# Revit family: Neo_Basin-Wall_Mounted-Neo_Metro-8936-EB
name_source: partatom
category: Plumbing Fixtures
units: mm (PartAtom-declared; Revit-internal decimal feet)

## family parameters
Cut with Voids When Loaded = No
Host = Face
OmniClass Number = 23.45.05.14.14
OmniClass Title = Sinks/Lavatories
Part Type = Normal
Room Calculation Point = No
Round Connector Dimension = Use Diameter
Shared = Yes

## types (1)
- 8936-EB
    8936 - NEO-BASIN (with NO Side Shelves), Satin Finish Stainless Steel = No
    8936-EB - NEO-BASIN with Enclosed Bottom, Entire Unit is Satin Finish Stainless Steel = Yes
    8936-HP - NEO-BASIN (with NO Side Shelves), Mira Finish Stainless Steel = No
    8936-HP-EB - NEO-BASIN with Enclosed Bottom, Entire Unit is Mira Finish Stainless Steel = No
    ADA Compliant = Yes
    Assembly Code = D2010440
    Basin Depth = 7"
    Basin Height = 5"
    Basin Width = 19"
    CW Connection = Yes
    CWFU = 1.5
    Cold Water Connection Diameter = 1/2"
    Compliance Certifications = ASME A112.18.1, CSA B125.1, cUPC
    Default Elevation = 34"
    Description = Neo-Basin Stainless Steel, Wall-Mounted Sink
    Finish = Stainless Steel-Neo Metro-Satin
    H0 - Less Punching (Will use wall-mounted faucet) = Yes
    H1 - Single Hole = No
    H38 - 8" (203mm) Center Set = No
    HW Connection = Yes
    HWFU = 1.5
    Hot Water Connection Diameter = 1/2"
    Installation Instruction Link = https://www.neo-metro.com
    Installation Type = Wall Mounted
    Manufacturer = Neo Metro
    Material = Stainless Steel-Neo Metro-Satin
    Model = 8936-EB
    OF - Option - Overflow Outlet = No
    Product Documentation Link = https://www.neo-metro.com
    Product Page URL = https://www.neo-metro.com
    Sink Back Height = 9 1/4"
    Sink Base Length = 6 1/2"
    Sink Base Width = 4 7/8"
    Sink Height = 17"
    Sink Length = 18 5/8"
    URL = https://www.neo-metro.com
    Vent Connection = No
    WFU = 2
    Waste Connection = Yes
    Waste Connection Diameter = 1 1/2"
    Waste Outlet Height = 11"

## geometry (parser evidence)
native form markers: Sweep x3
no freeform markers — native parametric forms only
